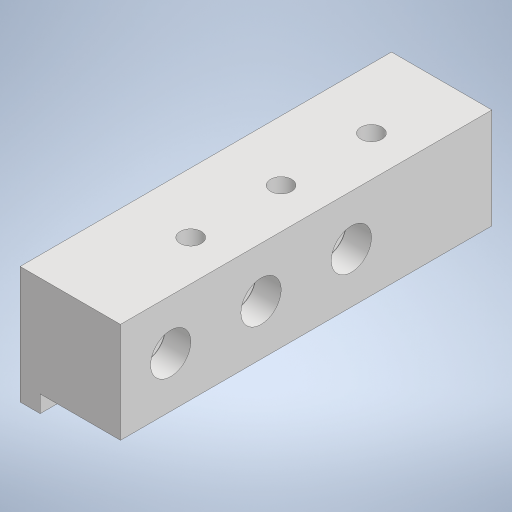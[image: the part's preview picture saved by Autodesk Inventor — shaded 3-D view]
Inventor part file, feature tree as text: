
AUTODESK INVENTOR PART (.ipt)
format: ipt  version: 2024.1 (Build 281209000, 209)  size: 279,552 bytes
history: native  units: in
note: dims shown in document units (in); Inventor stores cm internally (conversion verified against a paired STEP export)
features: extrude x7, sketch x7, chamfer x1
ambient origin geometry x8: Origin, YZ Plane, XZ Plane, XY Plane, X Axis, Y Axis, Z Axis, Center Point
bodies: Solid1 (feature_tree)
feature tree (15):
  extrude  "Extrusion1"  Depth=0.3937in
  extrude  "Extrusion2"  Depth=0.0787in
  extrude  "Extrusion3"  Depth=0.0669in
  extrude  "Extrusion4"  Depth=0.315in
  extrude  "Extrusion5"  Depth=0.1575in
  chamfer  "Chamfer1"  [1 undecoded]
  extrude  "Extrusion6"  Depth=0.315in
  extrude  "Extrusion7"  Depth=0.315in
  sketch  "Sketch1"  dims[d0=1.1024in d1=0.3937in]
  sketch  "Sketch2"  dims[d2=0.3937in d3=0.0in d4=0.0787in]
  sketch  "Sketch3"  dims[d5=0.0669in d6=0.0in d7=0.0827in]
  sketch  "Sketch4"  dims[d8=0.0827in d9=0.315in]
  sketch  "Sketch5"  dims[d10=0.3543in d11=0.1575in]
  sketch  "Sketch6"  dims[d12=0.1575in d13=0.0in d14=0.0in]
  sketch  "Sketch7"  dims[d15=0.0827in d16=0.0827in d17=0.0827in d18=0.1969in d19=0.1969in d20=0.1969in d21=0.1969in d22=0.3543in d23=0.3543in d24=0.0in d25=0.0in d26=0.1575in d27=0.1575in d28=0.1575in d29=0.0984in d30=0.0in d31=0.0354in d32=0.0787in d33=45.0deg d34=0.3543in d35=0.0in d39=0.0827in d40=0.1575in d41=0.315in d42=0.0in d43=0.0in]
note: 1 required parameter value undecoded (feature->parameter linkage not recoverable at this tier; creation-order binding heuristic only, values carry confidence <= 0.55)
